# Revit family: Landscaping_Other_Axelent_Bike-Up_Pole_171092
name_source: partatom
category: Furniture
revit_build: Autodesk Revit 2018 (Build: 20190510_1515(x64)
units: mm (PartAtom-declared; Revit-internal decimal feet)

## family parameters
Always vertical = Yes
Cut with Voids When Loaded = No
OmniClass Number = 23.40.10.14
OmniClass Title = Exterior Specialties
Room Calculation Point = No
Shared = No
Work Plane-Based = No

## types (1)
- Bike-Up Pole 1 bike
    AssetType = Fixed
    BIMObjectName = Landscaping_Other_Axelent_Bike-Up_Pole_171092
    Brand = Axelent
    Category = Cycle lockers
    Color = Grey
    Cost = 0 $
    CycleBollardMainMaterial = Steel, Galvanized
    Description = Bicycle rack Bike-Up Pole 1 bike is a bicycle rack with space for a bicycle on the ground, and can be easily placed along e.g. sidewalks. The stand is mounted by screwing it into the ground.
    DurationUnit = Years
    IfcExportAs = IfcFurnishingElementType
    IfcExportType = BOLLARD
    MainColor = Grey
    Manufacturer = Axelent
    ManufacturerName = Axelent
    ManufacturerURL = https://www.axelent.com
    Material = Hot-dip galvanized
    Model = Bike-Up Pole 1 bike
    ModelNumber = 171092
    NBSDescription = Aluminium cycle lockers
    NBSReference = 45-35-86/311
    Name = Bike-Up_Pole_171092
    NominalDepth = 263 mm
    NominalHeight = 560 mm
    NominalLength = 150 mm
    ProductDatasheet = https://www.axelent.com
    ProductInformation = Bicycle rack Bike-Up Pole 1 bike is a bicycle rack with space for a bicycle on the ground, and can be easily placed along e.g. sidewalks. The stand is mounted by screwing it into the ground.
    Shape = Sculptured
    Size = 150x263x560 mm
    URL = https://www.axelent.com
    Uniclass2 = Pr_40_30_20
    Uniclass2015Description = Cycle stands and lockers
    Uniclass2015Reference = Pr_40_30_21
    Version = 1
    VersionDate = 22/07/2021
    WarrantyDurationUnit = Years

## geometry (parser evidence)
native form markers: Sweep x5
no freeform markers — native parametric forms only
